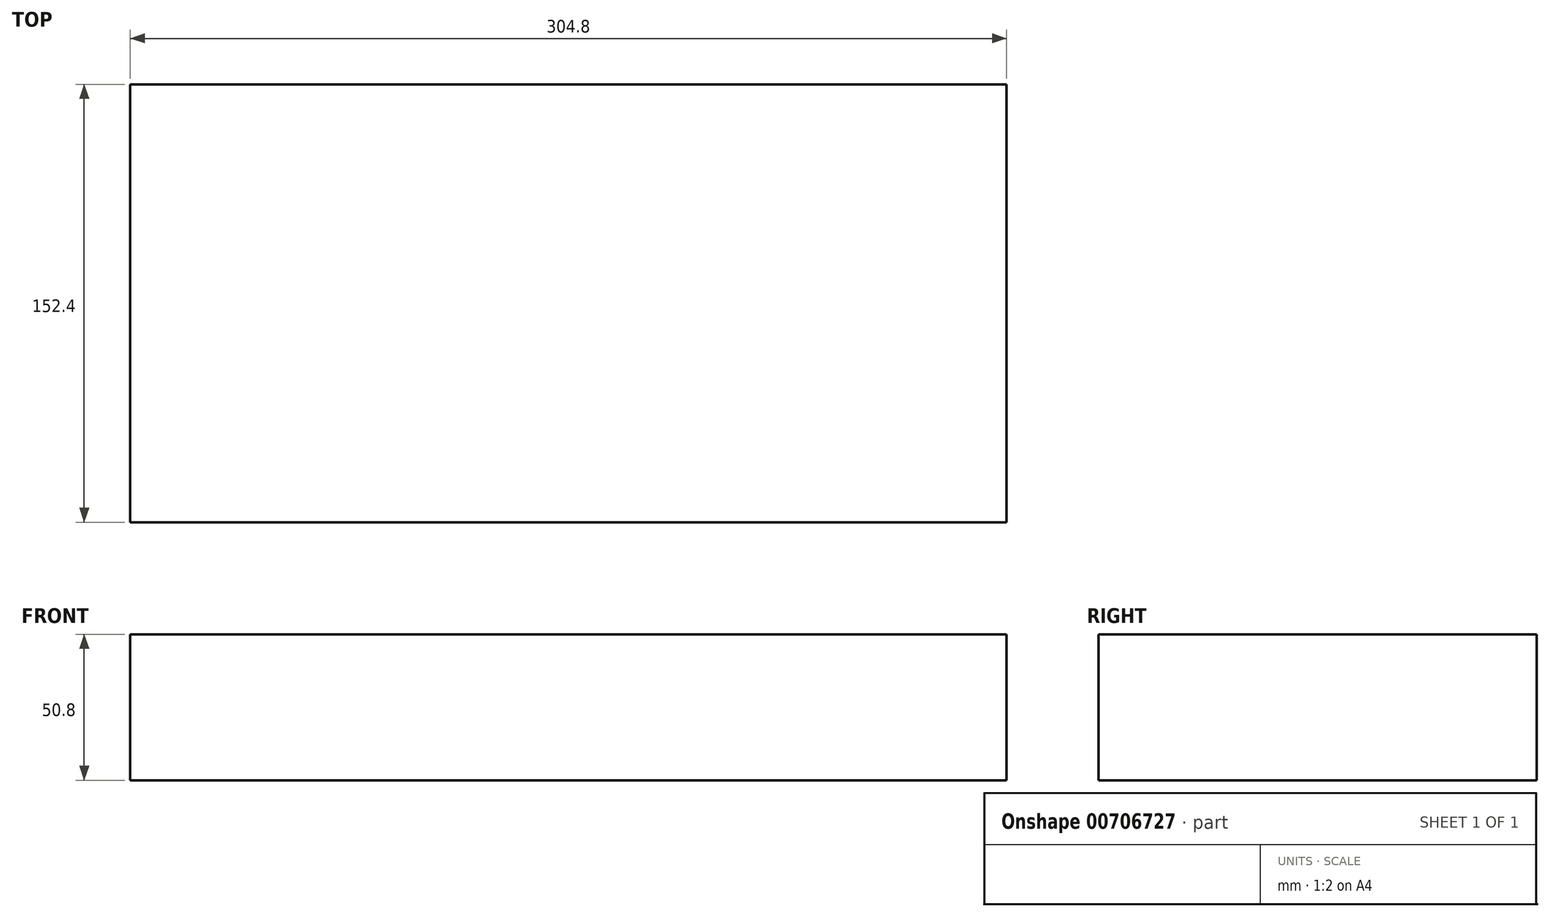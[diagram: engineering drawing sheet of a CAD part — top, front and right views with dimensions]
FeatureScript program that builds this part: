
annotation { "Feature Type Name" : "Feature", "Feature Type Description" : "" }
export const myFeature = defineFeature(function(context is Context, id is Id, definition is map)
    precondition{}
    {
        {
            var Q0;
            Q0=qCreatedBy(makeId("Top.planeOp"),FACE);
            var sketch = newSketch(context, id + "F0", { "sketchPlane" : qUnion([Q0])});
            skLineSegment(sketch, "E0.bottom", {"start": v(152.4, 76.2) * mm, "end": v(-152.4, 76.2) * mm});
            skLineSegment(sketch, "E0.top", {"start": v(152.4, -76.2) * mm, "end": v(-152.4, -76.2) * mm});
            skLineSegment(sketch, "E0.left", {"start": v(152.4, 76.2) * mm, "end": v(152.4, -76.2) * mm});
            skLineSegment(sketch, "E0.right", {"start": v(-152.4, 76.2) * mm, "end": v(-152.4, -76.2) * mm});
            skPoint(sketch, "E0.middle", {"position": v(0, 0) * mm});
            skSolve(sketch);
        }
        {
            var Q0;
            Q0=makeQuery(id+"F0.imprint","IMPRINT",FACE,{"disambiguationData":[TD([[makeQuery(id+"F0.imprint","IMPRINT",EDGE,{"derivedFrom":sQuery(id+"F0.wireOp",EDGE,"E0.bottom")}),1.0]])]});
            extrude(context, id + "F1", {"entities" : qUnion([Q0]), "depth" : 50.8 * mm, "offsetDistance" : 25.4 * mm});
        }
    });
